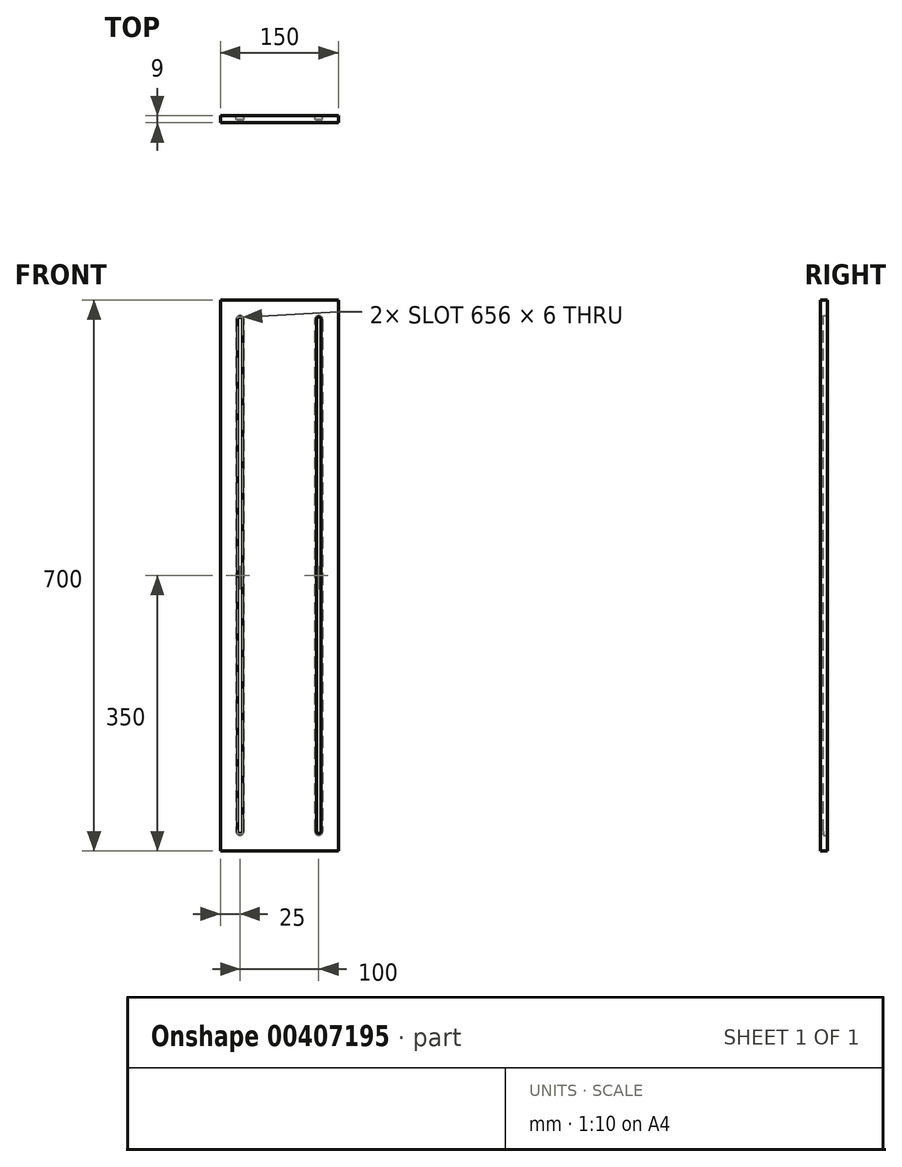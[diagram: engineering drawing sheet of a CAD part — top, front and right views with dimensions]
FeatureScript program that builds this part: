
annotation { "Feature Type Name" : "Feature", "Feature Type Description" : "" }
export const myFeature = defineFeature(function(context is Context, id is Id, definition is map)
    precondition{}
    {
        {
            var Q0;
            Q0=qCreatedBy(makeId("Front.planeOp"),FACE);
            var sketch = newSketch(context, id + "F0", { "sketchPlane" : qUnion([Q0])});
            skLineSegment(sketch, "E0.bottom", {"start": v(88.83, 9) * mm, "end": v(-61.17, 9) * mm});
            skLineSegment(sketch, "E0.top", {"start": v(88.83, 709) * mm, "end": v(-61.17, 709) * mm});
            skLineSegment(sketch, "E0.left", {"start": v(88.83, 9) * mm, "end": v(88.83, 709) * mm});
            skLineSegment(sketch, "E0.right", {"start": v(-61.17, 9) * mm, "end": v(-61.17, 709) * mm});
            skPoint(sketch, "E0.middle", {"position": v(0, 0) * mm});
            skSolve(sketch);
        }
        {
            var Q0;
            Q0 = qSketchRegion(id + "F0", true);
            var Q1;
            Q1 = qConstructionFilter(qBodyType(qCreatedBy(id + "F0" ,EDGE), BodyType.WIRE), ConstructionObject.NO);
            extrude(context, id + "F1", {"entities" : qUnion([Q0]), "surfaceEntities" : qUnion([Q1]), "endBound" : BoundingType.SYMMETRIC, "depth" : 9 * mm});
        }
        {
            var Q0;
            {var subQ0=sQuery(id+"F0.wireOp",EDGE,"E0.top");var subQ1=sQuery(id+"F0.wireOp",EDGE,"E0.left");var subQ2=sQuery(id+"F0.wireOp",EDGE,"E0.right");Q0=makeQuery(id+"FY4suBFZRrI5oW9_1.boolean.opBoolean","SPLIT",FACE,{"disambiguationData":[TD([makeQuery(id+"F1.opExtrude","SWEPT_FACE",FACE,{"disambiguationData":[OSD([subQ0])]})])],"derivedFrom":makeQuery(id+"F1.opExtrude","CAP_FACE",FACE,{"disambiguationData":[OSD([sQuery(id+"F0.wireOp",EDGE,"E0.bottom"),subQ0,subQ1,subQ2])],"isStart":false})});}
            var sketch = newSketch(context, id + "F2", { "sketchPlane" : qUnion([Q0])});
            skCircle(sketch, "E1", {"center": v(-36.17, 684) * mm, "radius": 3 * mm});
            skCircle(sketch, "E2", {"center": v(63.83, 684) * mm, "radius": 3 * mm});
            skCircle(sketch, "E3", {"center": v(-36.17, 34) * mm, "radius": 3 * mm});
            skCircle(sketch, "E4", {"center": v(63.83, 34) * mm, "radius": 3 * mm});
            skLineSegment(sketch, "E5.bottom", {"start": v(-36.17, 684) * mm, "end": v(63.83, 684) * mm, "construction": true});
            skLineSegment(sketch, "E5.top", {"start": v(-36.17, 34) * mm, "end": v(63.83, 34) * mm, "construction": true});
            skLineSegment(sketch, "E5.left", {"start": v(-36.17, 684) * mm, "end": v(-36.17, 34) * mm, "construction": true});
            skLineSegment(sketch, "E5.right", {"start": v(63.83, 684) * mm, "end": v(63.83, 34) * mm, "construction": true});
            skLineSegment(sketch, "E6", {"start": v(66.83, 684) * mm, "end": v(66.83, 34) * mm});
            skLineSegment(sketch, "E7", {"start": v(60.83, 34) * mm, "end": v(60.83, 684) * mm});
            skLineSegment(sketch, "E8", {"start": v(-39.17, 684) * mm, "end": v(-39.17, 34) * mm});
            skLineSegment(sketch, "E9", {"start": v(-33.17, 34) * mm, "end": v(-33.17, 684) * mm});
            skSolve(sketch);
        }
        {
            var Q0;
            Q0 = qSketchRegion(id + "F2", true);
            extrude(context, id + "F3", {"entities" : qUnion([Q0]), "operationType" : NewBodyOperationType.REMOVE, "endBound" : BoundingType.THROUGH_ALL, "oppositeDirection" : true, "depth" : 25 * mm});
        }
        {
            var Q0;
            Q0=makeQuery(id+"F1.opExtrude","CAP_FACE",FACE,{"disambiguationData":[OSD([sQuery(id+"F0.wireOp",EDGE,"E0.bottom"),sQuery(id+"F0.wireOp",EDGE,"E0.top"),sQuery(id+"F0.wireOp",EDGE,"E0.left"),sQuery(id+"F0.wireOp",EDGE,"E0.right")])],"isStart":true});
            var sketch = newSketch(context, id + "F4", { "sketchPlane" : qUnion([Q0])});
            skLineSegment(sketch, "E10.0", {"start": v(31.17, 34) * mm, "end": v(31.17, 684) * mm});
            skArc(sketch, "E10.1", {"start": v(41.17, 34) * mm, "mid": v(36.17, 29) * mm, "end": v(31.17, 34) * mm});
            skLineSegment(sketch, "E10.2", {"start": v(41.17, 684) * mm, "end": v(41.17, 34) * mm});
            skArc(sketch, "E10.3", {"start": v(31.17, 684) * mm, "mid": v(36.17, 689) * mm, "end": v(41.17, 684) * mm});
            skLineSegment(sketch, "E11.0", {"start": v(-58.83, 34) * mm, "end": v(-58.83, 684) * mm});
            skArc(sketch, "E11.1", {"start": v(-58.83, 34) * mm, "mid": v(-63.83, 29) * mm, "end": v(-68.83, 34) * mm});
            skLineSegment(sketch, "E11.2", {"start": v(-68.83, 684) * mm, "end": v(-68.83, 34) * mm});
            skArc(sketch, "E11.3", {"start": v(-68.83, 684) * mm, "mid": v(-63.83, 689) * mm, "end": v(-58.83, 684) * mm});
            skSolve(sketch);
        }
        {
            var Q0;
            Q0 = qSketchRegion(id + "F4", true);
            extrude(context, id + "F5", {"entities" : qUnion([Q0]), "operationType" : NewBodyOperationType.REMOVE, "oppositeDirection" : true, "depth" : 5 * mm});
        }
    });
